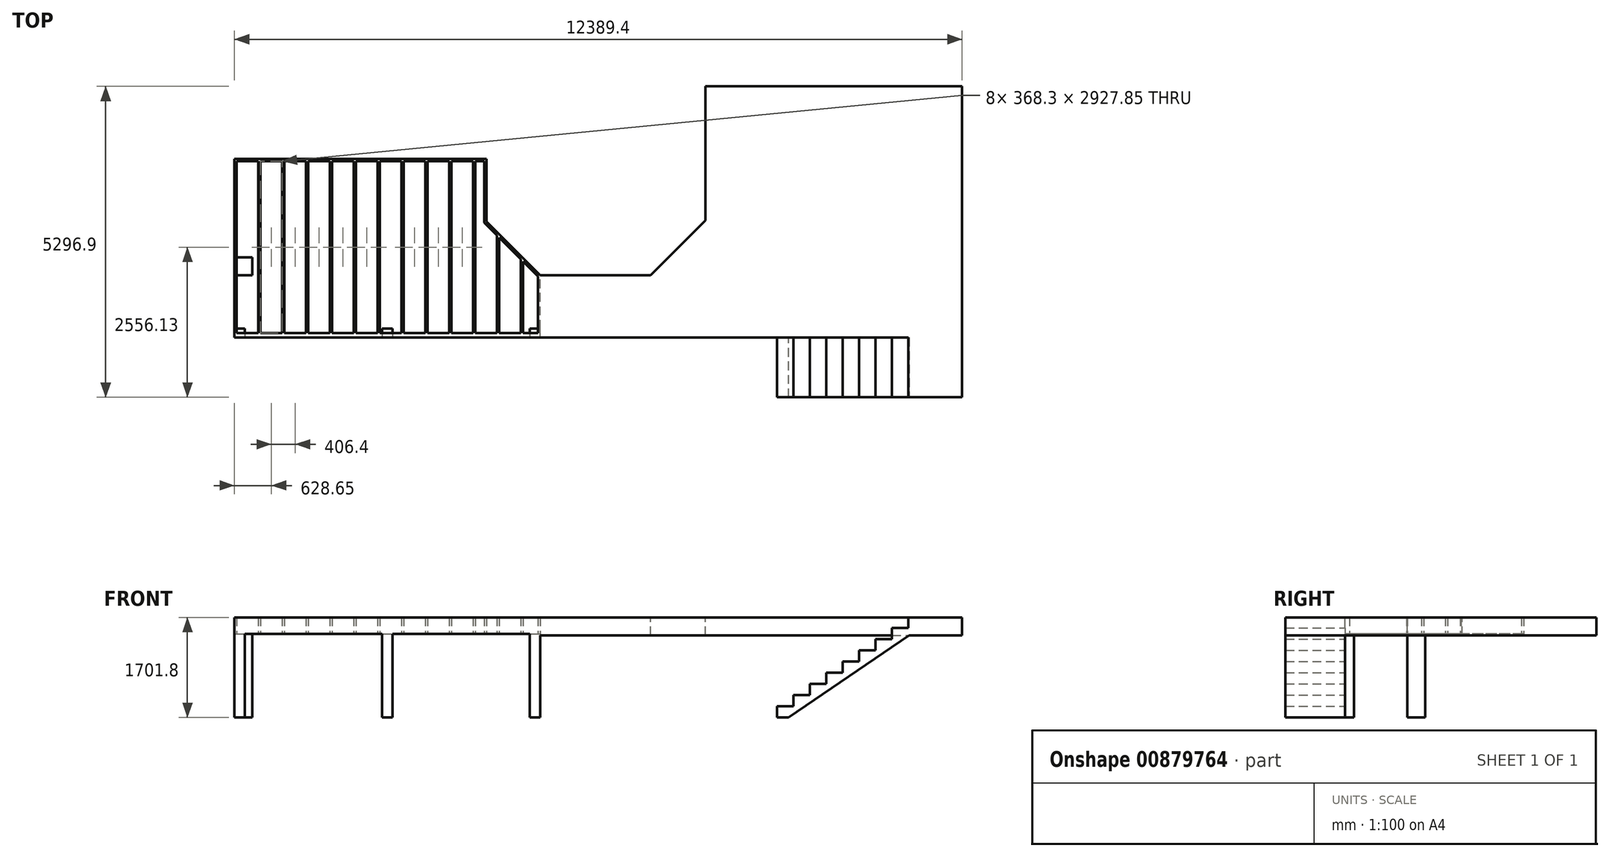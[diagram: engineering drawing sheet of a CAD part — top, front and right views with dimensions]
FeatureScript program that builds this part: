
annotation { "Feature Type Name" : "Feature", "Feature Type Description" : "" }
export const myFeature = defineFeature(function(context is Context, id is Id, definition is map)
    precondition{}
    {
        {
            var Q0;
            Q0=qCreatedBy(makeId("Top.planeOp"),FACE);
            var sketch = newSketch(context, id + "F0", { "sketchPlane" : qUnion([Q0])});
            skLineSegment(sketch, "E0.bottom", {"start": v(0, -1676.4) * mm, "end": v(304.8, -1676.4) * mm});
            skLineSegment(sketch, "E0.top", {"start": v(0, -1981.2) * mm, "end": v(304.8, -1981.2) * mm});
            skLineSegment(sketch, "E0.left", {"start": v(0, -1676.4) * mm, "end": v(0, -1981.2) * mm});
            skLineSegment(sketch, "E0.right", {"start": v(304.8, -1676.4) * mm, "end": v(304.8, -1981.2) * mm});
            skLineSegment(sketch, "E1.bottom", {"start": v(0, -2889.75) * mm, "end": v(177.8, -2889.75) * mm});
            skLineSegment(sketch, "E1.top", {"start": v(0, -3042.15) * mm, "end": v(177.8, -3042.15) * mm});
            skLineSegment(sketch, "E1.left", {"start": v(0, -2889.75) * mm, "end": v(0, -3042.15) * mm});
            skLineSegment(sketch, "E1.right", {"start": v(177.8, -2889.75) * mm, "end": v(177.8, -3042.15) * mm});
            skLineSegment(sketch, "E2.bottom", {"start": v(2514.6, -2889.75) * mm, "end": v(2692.4, -2889.75) * mm});
            skLineSegment(sketch, "E2.top", {"start": v(2514.6, -3042.15) * mm, "end": v(2692.4, -3042.15) * mm});
            skLineSegment(sketch, "E2.left", {"start": v(2514.6, -2889.75) * mm, "end": v(2514.6, -3042.15) * mm});
            skLineSegment(sketch, "E2.right", {"start": v(2692.4, -2889.75) * mm, "end": v(2692.4, -3042.15) * mm});
            skLineSegment(sketch, "E3.bottom", {"start": v(5029.2, -2889.75) * mm, "end": v(5207, -2889.75) * mm});
            skLineSegment(sketch, "E3.top", {"start": v(5029.2, -3042.15) * mm, "end": v(5207, -3042.15) * mm});
            skLineSegment(sketch, "E3.left", {"start": v(5029.2, -2889.75) * mm, "end": v(5029.2, -3042.15) * mm});
            skLineSegment(sketch, "E3.right", {"start": v(5207, -2889.75) * mm, "end": v(5207, -3042.15) * mm});
            skLineSegment(sketch, "E4", {"start": v(0, 0) * mm, "end": v(4292.6, 0) * mm, "construction": true});
            skLineSegment(sketch, "E5", {"start": v(4292.6, 0) * mm, "end": v(4292.6, -1066.8) * mm, "construction": true});
            skLineSegment(sketch, "E6", {"start": v(4292.6, -1066.8) * mm, "end": v(5226.55, -2000.75) * mm, "construction": true});
            skLineSegment(sketch, "E7", {"start": v(5226.55, -2000.75) * mm, "end": v(7106.15, -2000.75) * mm, "construction": true});
            skSolve(sketch);
        }
        {
            var Q0;
            Q0=qSketchRegion(id+"F0",true);
            extrude(context, id + "F1", {"entities" : qUnion([Q0]), "depth" : 1422.4 * mm, "offsetDistance" : 25.4 * mm});
        }
        {
            var Q0;
            Q0=makeQuery(id+"F1.opExtrude","CAP_FACE",FACE,{"disambiguationData":[OSD([sQuery(id+"F0.wireOp",EDGE,"E0.bottom"),sQuery(id+"F0.wireOp",EDGE,"E0.top"),sQuery(id+"F0.wireOp",EDGE,"E0.left"),sQuery(id+"F0.wireOp",EDGE,"E0.right")])],"isStart":false});
            var sketch = newSketch(context, id + "F2", { "sketchPlane" : qUnion([Q0])});
            skLineSegment(sketch, "E8.0", {"start": v(0, 0) * mm, "end": v(4292.6, 0) * mm});
            skLineSegment(sketch, "E9.0", {"start": v(4292.6, 0) * mm, "end": v(4292.6, -1066.8) * mm});
            skLineSegment(sketch, "E9.1", {"start": v(4292.6, -1066.8) * mm, "end": v(5207, -1981.2) * mm});
            skLineSegment(sketch, "E10", {"start": v(0, 0) * mm, "end": v(0, -3042.15) * mm});
            skLineSegment(sketch, "E11", {"start": v(0, -3042.15) * mm, "end": v(5207, -3042.15) * mm});
            skLineSegment(sketch, "E12", {"start": v(5207, -3042.15) * mm, "end": v(5207, -1981.2) * mm});
            skPoint(sketch, "E13.orphan", {"position": v(5226.55, -2000.75) * mm});
            skLineSegment(sketch, "E14.0", {"start": v(4254.5, -38.1) * mm, "end": v(4254.5, -1082.58) * mm});
            skLineSegment(sketch, "E14.1", {"start": v(5168.9, -3004.05) * mm, "end": v(5168.9, -1996.98) * mm});
            skLineSegment(sketch, "E14.2", {"start": v(38.1, -3004.05) * mm, "end": v(5168.9, -3004.05) * mm});
            skLineSegment(sketch, "E14.3", {"start": v(4254.5, -1082.58) * mm, "end": v(5168.9, -1996.98) * mm});
            skLineSegment(sketch, "E14.4", {"start": v(38.1, -38.1) * mm, "end": v(38.1, -3004.05) * mm});
            skLineSegment(sketch, "E14.5", {"start": v(38.1, -38.1) * mm, "end": v(4254.5, -38.1) * mm});
            skSolve(sketch);
        }
        {
            var Q0;
            Q0=qSketchRegion(id+"F2",true);
            extrude(context, id + "F3", {"entities" : qUnion([Q0]), "operationType" : NewBodyOperationType.ADD, "depth" : 279.4 * mm, "offsetDistance" : 25.4 * mm});
        }
        {
            var Q0;
            Q0=makeQuery(id+"F1.opExtrude","CAP_FACE",FACE,{"disambiguationData":[OSD([sQuery(id+"F0.wireOp",EDGE,"E1.bottom"),sQuery(id+"F0.wireOp",EDGE,"E1.top"),sQuery(id+"F0.wireOp",EDGE,"E1.left"),sQuery(id+"F0.wireOp",EDGE,"E1.right")])],"isStart":false});
            var sketch = newSketch(context, id + "F4", { "sketchPlane" : qUnion([Q0])});
            skPoint(sketch, "E15.oppositeSnap0", {"position": v(38.1, -2965.95) * mm});
            skLineSegment(sketch, "E15.bottom", {"start": v(38.1, -3004.05) * mm, "end": v(5168.9, -3004.05) * mm});
            skLineSegment(sketch, "E15.top", {"start": v(38.1, -2965.95) * mm, "end": v(5168.9, -2965.95) * mm});
            skLineSegment(sketch, "E15.left", {"start": v(38.1, -3004.05) * mm, "end": v(38.1, -2965.95) * mm});
            skLineSegment(sketch, "E15.right", {"start": v(5168.9, -3004.05) * mm, "end": v(5168.9, -2965.95) * mm});
            skSolve(sketch);
        }
        {
            var Q0;
            Q0=qSketchRegion(id+"F4",true);
            var Q1;
            Q1=makeQuery(id+"F3.opExtrude","CAP_FACE",FACE,{"disambiguationData":[OSD([sQuery(id+"F2.wireOp",EDGE,"E8.0"),sQuery(id+"F2.wireOp",EDGE,"E9.0"),sQuery(id+"F2.wireOp",EDGE,"E9.1"),sQuery(id+"F2.wireOp",EDGE,"E10"),sQuery(id+"F2.wireOp",EDGE,"E11"),sQuery(id+"F2.wireOp",EDGE,"E12"),sQuery(id+"F2.wireOp",EDGE,"E14.0"),sQuery(id+"F2.wireOp",EDGE,"E14.1"),sQuery(id+"F2.wireOp",EDGE,"E14.2"),sQuery(id+"F2.wireOp",EDGE,"E14.3"),sQuery(id+"F2.wireOp",EDGE,"E14.4"),sQuery(id+"F2.wireOp",EDGE,"E14.5")])],"isStart":false});
            extrude(context, id + "F5", {"entities" : qUnion([Q0]), "operationType" : NewBodyOperationType.ADD, "endBound" : BoundingType.UP_TO_SURFACE, "depth" : 25.4 * mm, "endBoundEntityFace" : qUnion([Q1]), "offsetDistance" : 25.4 * mm});
        }
        {
            var Q0;
            Q0=makeQuery(id+"F1.opExtrude","CAP_FACE",FACE,{"disambiguationData":[OSD([sQuery(id+"F0.wireOp",EDGE,"E0.bottom"),sQuery(id+"F0.wireOp",EDGE,"E0.top"),sQuery(id+"F0.wireOp",EDGE,"E0.left"),sQuery(id+"F0.wireOp",EDGE,"E0.right")])],"isStart":false});
            var sketch = newSketch(context, id + "F6", { "sketchPlane" : qUnion([Q0])});
            skLineSegment(sketch, "E16.bottom", {"start": v(406.4, -38.1) * mm, "end": v(444.5, -38.1) * mm});
            skLineSegment(sketch, "E16.top", {"start": v(406.4, -2965.95) * mm, "end": v(444.5, -2965.95) * mm});
            skLineSegment(sketch, "E16.left", {"start": v(406.4, -38.1) * mm, "end": v(406.4, -2965.95) * mm});
            skLineSegment(sketch, "E16.right", {"start": v(444.5, -38.1) * mm, "end": v(444.5, -2965.95) * mm});
            skLineSegment(sketch, "E17.1.0.0", {"start": v(850.9, -38.1) * mm, "end": v(850.9, -2965.95) * mm});
            skLineSegment(sketch, "E17.1.0.1", {"start": v(812.8, -38.1) * mm, "end": v(812.8, -2965.95) * mm});
            skLineSegment(sketch, "E17.1.0.2", {"start": v(812.8, -38.1) * mm, "end": v(850.9, -38.1) * mm});
            skLineSegment(sketch, "E17.1.0.3", {"start": v(812.8, -2965.95) * mm, "end": v(850.9, -2965.95) * mm});
            skLineSegment(sketch, "E17.2.0.0", {"start": v(1257.3, -38.1) * mm, "end": v(1257.3, -2965.95) * mm});
            skLineSegment(sketch, "E17.2.0.1", {"start": v(1219.2, -38.1) * mm, "end": v(1219.2, -2965.95) * mm});
            skLineSegment(sketch, "E17.2.0.2", {"start": v(1219.2, -38.1) * mm, "end": v(1257.3, -38.1) * mm});
            skLineSegment(sketch, "E17.2.0.3", {"start": v(1219.2, -2965.95) * mm, "end": v(1257.3, -2965.95) * mm});
            skLineSegment(sketch, "E17.3.0.0", {"start": v(1663.7, -38.1) * mm, "end": v(1663.7, -2965.95) * mm});
            skLineSegment(sketch, "E17.3.0.1", {"start": v(1625.6, -38.1) * mm, "end": v(1625.6, -2965.95) * mm});
            skLineSegment(sketch, "E17.3.0.2", {"start": v(1625.6, -38.1) * mm, "end": v(1663.7, -38.1) * mm});
            skLineSegment(sketch, "E17.3.0.3", {"start": v(1625.6, -2965.95) * mm, "end": v(1663.7, -2965.95) * mm});
            skLineSegment(sketch, "E17.4.0.0", {"start": v(2070.1, -38.1) * mm, "end": v(2070.1, -2965.95) * mm});
            skLineSegment(sketch, "E17.4.0.1", {"start": v(2032, -38.1) * mm, "end": v(2032, -2965.95) * mm});
            skLineSegment(sketch, "E17.4.0.2", {"start": v(2032, -38.1) * mm, "end": v(2070.1, -38.1) * mm});
            skLineSegment(sketch, "E17.4.0.3", {"start": v(2032, -2965.95) * mm, "end": v(2070.1, -2965.95) * mm});
            skLineSegment(sketch, "E17.5.0.0", {"start": v(2476.5, -38.1) * mm, "end": v(2476.5, -2965.95) * mm});
            skLineSegment(sketch, "E17.5.0.1", {"start": v(2438.4, -38.1) * mm, "end": v(2438.4, -2965.95) * mm});
            skLineSegment(sketch, "E17.5.0.2", {"start": v(2438.4, -38.1) * mm, "end": v(2476.5, -38.1) * mm});
            skLineSegment(sketch, "E17.5.0.3", {"start": v(2438.4, -2965.95) * mm, "end": v(2476.5, -2965.95) * mm});
            skLineSegment(sketch, "E17.6.0.0", {"start": v(2882.9, -38.1) * mm, "end": v(2882.9, -2965.95) * mm});
            skLineSegment(sketch, "E17.6.0.1", {"start": v(2844.8, -38.1) * mm, "end": v(2844.8, -2965.95) * mm});
            skLineSegment(sketch, "E17.6.0.2", {"start": v(2844.8, -38.1) * mm, "end": v(2882.9, -38.1) * mm});
            skLineSegment(sketch, "E17.6.0.3", {"start": v(2844.8, -2965.95) * mm, "end": v(2882.9, -2965.95) * mm});
            skLineSegment(sketch, "E17.7.0.0", {"start": v(3289.3, -38.1) * mm, "end": v(3289.3, -2965.95) * mm});
            skLineSegment(sketch, "E17.7.0.1", {"start": v(3251.2, -38.1) * mm, "end": v(3251.2, -2965.95) * mm});
            skLineSegment(sketch, "E17.7.0.2", {"start": v(3251.2, -38.1) * mm, "end": v(3289.3, -38.1) * mm});
            skLineSegment(sketch, "E17.7.0.3", {"start": v(3251.2, -2965.95) * mm, "end": v(3289.3, -2965.95) * mm});
            skLineSegment(sketch, "E17.8.0.0", {"start": v(3695.7, -38.1) * mm, "end": v(3695.7, -2965.95) * mm});
            skLineSegment(sketch, "E17.8.0.1", {"start": v(3657.6, -38.1) * mm, "end": v(3657.6, -2965.95) * mm});
            skLineSegment(sketch, "E17.8.0.2", {"start": v(3657.6, -38.1) * mm, "end": v(3695.7, -38.1) * mm});
            skLineSegment(sketch, "E17.8.0.3", {"start": v(3657.6, -2965.95) * mm, "end": v(3695.7, -2965.95) * mm});
            skLineSegment(sketch, "E17.9.0.0", {"start": v(4102.1, -38.1) * mm, "end": v(4102.1, -2965.95) * mm});
            skLineSegment(sketch, "E17.9.0.1", {"start": v(4064, -38.1) * mm, "end": v(4064, -2965.95) * mm});
            skLineSegment(sketch, "E17.9.0.2", {"start": v(4064, -38.1) * mm, "end": v(4102.1, -38.1) * mm});
            skLineSegment(sketch, "E17.9.0.3", {"start": v(4064, -2965.95) * mm, "end": v(4102.1, -2965.95) * mm});
            skLineSegment(sketch, "E17.direction1", {"start": v(406.4, -2965.95) * mm, "end": v(812.8, -2965.95) * mm, "construction": true});
            skLineSegment(sketch, "E18.top", {"start": v(4470.4, -2965.95) * mm, "end": v(4508.5, -2965.95) * mm});
            skLineSegment(sketch, "E18.left", {"start": v(4470.4, -1298.48) * mm, "end": v(4470.4, -2965.95) * mm});
            skLineSegment(sketch, "E18.right", {"start": v(4508.5, -1336.58) * mm, "end": v(4508.5, -2965.95) * mm});
            skLineSegment(sketch, "E19.top", {"start": v(4876.8, -2965.95) * mm, "end": v(4914.9, -2965.95) * mm});
            skLineSegment(sketch, "E19.left", {"start": v(4876.8, -1704.88) * mm, "end": v(4876.8, -2965.95) * mm});
            skLineSegment(sketch, "E19.right", {"start": v(4914.9, -1742.98) * mm, "end": v(4914.9, -2965.95) * mm});
            skLineSegment(sketch, "E20", {"start": v(4470.4, -1298.48) * mm, "end": v(4508.5, -1336.58) * mm});
            skLineSegment(sketch, "E21.trimOffspring", {"start": v(4876.8, -1704.88) * mm, "end": v(4914.9, -1742.98) * mm});
            skSolve(sketch);
        }
        {
            var Q0;
            Q0=qSketchRegion(id+"F6",true);
            var Q1;
            {var subQ0=sQuery(id+"F2.wireOp",EDGE,"E14.5");var subQ1=sQuery(id+"F2.wireOp",EDGE,"E14.4");var subQ2=sQuery(id+"F2.wireOp",EDGE,"E14.3");var subQ3=sQuery(id+"F2.wireOp",EDGE,"E14.2");var subQ4=sQuery(id+"F2.wireOp",EDGE,"E14.1");var subQ5=sQuery(id+"F2.wireOp",EDGE,"E14.0");var subQ6=sQuery(id+"F2.wireOp",EDGE,"E12");var subQ7=sQuery(id+"F2.wireOp",EDGE,"E11");var subQ8=sQuery(id+"F2.wireOp",EDGE,"E10");var subQ9=sQuery(id+"F2.wireOp",EDGE,"E9.1");var subQ10=sQuery(id+"F2.wireOp",EDGE,"E9.0");var subQ11=sQuery(id+"F2.wireOp",EDGE,"E8.0");Q1=makeQuery(id+"F5.boolean.opBoolean","MERGE",FACE,{"derivedFrom":[makeQuery(id+"F3.opExtrude","CAP_FACE",FACE,{"disambiguationData":[OSD([subQ11,subQ10,subQ9,subQ8,subQ7,subQ6,subQ5,subQ4,subQ3,subQ2,subQ1,subQ0])],"isStart":false}),makeQuery(id+"F5.opExtrude","CAP_FACE",FACE,{"disambiguationData":[OSD([subQ11,subQ10,subQ9,subQ8,subQ7,subQ6,subQ5,subQ4,subQ3,subQ2,subQ1,subQ0])],"isStart":false})]});}
            extrude(context, id + "F7", {"entities" : qUnion([Q0]), "operationType" : NewBodyOperationType.ADD, "endBound" : BoundingType.UP_TO_SURFACE, "depth" : 25.4 * mm, "endBoundEntityFace" : qUnion([Q1]), "offsetDistance" : 25.4 * mm});
        }
        {
            var Q0;
            Q0=makeQuery(id+"F7.boolean.opBoolean","MERGE",FACE,{"derivedFrom":[makeQuery(id+"F5.boolean.opBoolean","MERGE",FACE,{"derivedFrom":[makeQuery(id+"F3.opExtrude","CAP_FACE",FACE,{"disambiguationData":[OSD([sQuery(id+"F2.wireOp",EDGE,"E8.0"),sQuery(id+"F2.wireOp",EDGE,"E9.0"),sQuery(id+"F2.wireOp",EDGE,"E9.1"),sQuery(id+"F2.wireOp",EDGE,"E10"),sQuery(id+"F2.wireOp",EDGE,"E11"),sQuery(id+"F2.wireOp",EDGE,"E12"),sQuery(id+"F2.wireOp",EDGE,"E14.0"),sQuery(id+"F2.wireOp",EDGE,"E14.1"),sQuery(id+"F2.wireOp",EDGE,"E14.2"),sQuery(id+"F2.wireOp",EDGE,"E14.3"),sQuery(id+"F2.wireOp",EDGE,"E14.4"),sQuery(id+"F2.wireOp",EDGE,"E14.5")])],"isStart":false}),makeQuery(id+"F5.opExtrude","CAP_FACE",FACE,{"disambiguationData":[OSD([sQuery(id+"F4.wireOp",EDGE,"E15.bottom"),sQuery(id+"F4.wireOp",EDGE,"E15.top"),sQuery(id+"F4.wireOp",EDGE,"E15.left"),sQuery(id+"F4.wireOp",EDGE,"E15.right")])],"isStart":false})]}),makeQuery(id+"F7.opExtrude","CAP_FACE",FACE,{"disambiguationData":[OSD([sQuery(id+"F6.wireOp",EDGE,"E16.bottom"),sQuery(id+"F6.wireOp",EDGE,"E16.top"),sQuery(id+"F6.wireOp",EDGE,"E16.left"),sQuery(id+"F6.wireOp",EDGE,"E16.right")])],"isStart":false}),makeQuery(id+"F7.opExtrude","CAP_FACE",FACE,{"disambiguationData":[OSD([sQuery(id+"F6.wireOp",EDGE,"E17.1.0.0"),sQuery(id+"F6.wireOp",EDGE,"E17.1.0.1"),sQuery(id+"F6.wireOp",EDGE,"E17.1.0.2"),sQuery(id+"F6.wireOp",EDGE,"E17.1.0.3")])],"isStart":false}),makeQuery(id+"F7.opExtrude","CAP_FACE",FACE,{"disambiguationData":[OSD([sQuery(id+"F6.wireOp",EDGE,"E17.2.0.0"),sQuery(id+"F6.wireOp",EDGE,"E17.2.0.1"),sQuery(id+"F6.wireOp",EDGE,"E17.2.0.2"),sQuery(id+"F6.wireOp",EDGE,"E17.2.0.3")])],"isStart":false}),makeQuery(id+"F7.opExtrude","CAP_FACE",FACE,{"disambiguationData":[OSD([sQuery(id+"F6.wireOp",EDGE,"E17.3.0.0"),sQuery(id+"F6.wireOp",EDGE,"E17.3.0.1"),sQuery(id+"F6.wireOp",EDGE,"E17.3.0.2"),sQuery(id+"F6.wireOp",EDGE,"E17.3.0.3")])],"isStart":false}),makeQuery(id+"F7.opExtrude","CAP_FACE",FACE,{"disambiguationData":[OSD([sQuery(id+"F6.wireOp",EDGE,"E17.4.0.0"),sQuery(id+"F6.wireOp",EDGE,"E17.4.0.1"),sQuery(id+"F6.wireOp",EDGE,"E17.4.0.2"),sQuery(id+"F6.wireOp",EDGE,"E17.4.0.3")])],"isStart":false}),makeQuery(id+"F7.opExtrude","CAP_FACE",FACE,{"disambiguationData":[OSD([sQuery(id+"F6.wireOp",EDGE,"E17.5.0.0"),sQuery(id+"F6.wireOp",EDGE,"E17.5.0.1"),sQuery(id+"F6.wireOp",EDGE,"E17.5.0.2"),sQuery(id+"F6.wireOp",EDGE,"E17.5.0.3")])],"isStart":false}),makeQuery(id+"F7.opExtrude","CAP_FACE",FACE,{"disambiguationData":[OSD([sQuery(id+"F6.wireOp",EDGE,"E17.6.0.0"),sQuery(id+"F6.wireOp",EDGE,"E17.6.0.1"),sQuery(id+"F6.wireOp",EDGE,"E17.6.0.2"),sQuery(id+"F6.wireOp",EDGE,"E17.6.0.3")])],"isStart":false}),makeQuery(id+"F7.opExtrude","CAP_FACE",FACE,{"disambiguationData":[OSD([sQuery(id+"F6.wireOp",EDGE,"E17.7.0.0"),sQuery(id+"F6.wireOp",EDGE,"E17.7.0.1"),sQuery(id+"F6.wireOp",EDGE,"E17.7.0.2"),sQuery(id+"F6.wireOp",EDGE,"E17.7.0.3")])],"isStart":false}),makeQuery(id+"F7.opExtrude","CAP_FACE",FACE,{"disambiguationData":[OSD([sQuery(id+"F6.wireOp",EDGE,"E17.8.0.0"),sQuery(id+"F6.wireOp",EDGE,"E17.8.0.1"),sQuery(id+"F6.wireOp",EDGE,"E17.8.0.2"),sQuery(id+"F6.wireOp",EDGE,"E17.8.0.3")])],"isStart":false}),makeQuery(id+"F7.opExtrude","CAP_FACE",FACE,{"disambiguationData":[OSD([sQuery(id+"F6.wireOp",EDGE,"E17.9.0.0"),sQuery(id+"F6.wireOp",EDGE,"E17.9.0.1"),sQuery(id+"F6.wireOp",EDGE,"E17.9.0.2"),sQuery(id+"F6.wireOp",EDGE,"E17.9.0.3")])],"isStart":false}),makeQuery(id+"F7.opExtrude","CAP_FACE",FACE,{"disambiguationData":[OSD([sQuery(id+"F6.wireOp",EDGE,"E18.top"),sQuery(id+"F6.wireOp",EDGE,"E18.left"),sQuery(id+"F6.wireOp",EDGE,"E18.right"),sQuery(id+"F6.wireOp",EDGE,"E20")])],"isStart":false}),makeQuery(id+"F7.opExtrude","CAP_FACE",FACE,{"disambiguationData":[OSD([sQuery(id+"F6.wireOp",EDGE,"E19.top"),sQuery(id+"F6.wireOp",EDGE,"E19.left"),sQuery(id+"F6.wireOp",EDGE,"E19.right"),sQuery(id+"F6.wireOp",EDGE,"E21.trimOffspring")])],"isStart":false})]});
            var sketch = newSketch(context, id + "F8", { "sketchPlane" : qUnion([Q0])});
            skLineSegment(sketch, "E22", {"start": v(5207, -1981.2) * mm, "end": v(5207, -3042.15) * mm});
            skLineSegment(sketch, "E23", {"start": v(5207, -1981.2) * mm, "end": v(7086.6, -1981.2) * mm});
            skLineSegment(sketch, "E24", {"start": v(7086.6, -1981.2) * mm, "end": v(8020.55, -1047.25) * mm});
            skLineSegment(sketch, "E25", {"start": v(8020.55, -1047.25) * mm, "end": v(8020.55, 1238.75) * mm});
            skLineSegment(sketch, "E26", {"start": v(8020.55, 1238.75) * mm, "end": v(12389.35, 1238.75) * mm});
            skLineSegment(sketch, "E27", {"start": v(12389.35, 1238.75) * mm, "end": v(12389.35, -3042.15) * mm});
            skLineSegment(sketch, "E28", {"start": v(5207, -3042.15) * mm, "end": v(12389.35, -3042.15) * mm});
            skSolve(sketch);
        }
        {
            var Q0;
            Q0=qSketchRegion(id+"F8",true);
            extrude(context, id + "F9", {"entities" : qUnion([Q0]), "operationType" : NewBodyOperationType.ADD, "oppositeDirection" : true, "depth" : 304.8 * mm, "offsetDistance" : 25.4 * mm});
        }
        {
            var Q0;
            Q0=makeQuery(id+"F9.boolean.opBoolean","MERGE",FACE,{"derivedFrom":[makeQuery(id+"F7.boolean.opBoolean","MERGE",FACE,{"derivedFrom":[makeQuery(id+"F5.boolean.opBoolean","MERGE",FACE,{"derivedFrom":[makeQuery(id+"F3.opExtrude","CAP_FACE",FACE,{"disambiguationData":[OSD([sQuery(id+"F2.wireOp",EDGE,"E8.0"),sQuery(id+"F2.wireOp",EDGE,"E9.0"),sQuery(id+"F2.wireOp",EDGE,"E9.1"),sQuery(id+"F2.wireOp",EDGE,"E10"),sQuery(id+"F2.wireOp",EDGE,"E11"),sQuery(id+"F2.wireOp",EDGE,"E12"),sQuery(id+"F2.wireOp",EDGE,"E14.0"),sQuery(id+"F2.wireOp",EDGE,"E14.1"),sQuery(id+"F2.wireOp",EDGE,"E14.2"),sQuery(id+"F2.wireOp",EDGE,"E14.3"),sQuery(id+"F2.wireOp",EDGE,"E14.4"),sQuery(id+"F2.wireOp",EDGE,"E14.5")])],"isStart":false}),makeQuery(id+"F5.opExtrude","CAP_FACE",FACE,{"disambiguationData":[OSD([sQuery(id+"F4.wireOp",EDGE,"E15.bottom"),sQuery(id+"F4.wireOp",EDGE,"E15.top"),sQuery(id+"F4.wireOp",EDGE,"E15.left"),sQuery(id+"F4.wireOp",EDGE,"E15.right")])],"isStart":false})]}),makeQuery(id+"F7.opExtrude","CAP_FACE",FACE,{"disambiguationData":[OSD([sQuery(id+"F6.wireOp",EDGE,"E16.bottom"),sQuery(id+"F6.wireOp",EDGE,"E16.top"),sQuery(id+"F6.wireOp",EDGE,"E16.left"),sQuery(id+"F6.wireOp",EDGE,"E16.right")])],"isStart":false}),makeQuery(id+"F7.opExtrude","CAP_FACE",FACE,{"disambiguationData":[OSD([sQuery(id+"F6.wireOp",EDGE,"E17.1.0.0"),sQuery(id+"F6.wireOp",EDGE,"E17.1.0.1"),sQuery(id+"F6.wireOp",EDGE,"E17.1.0.2"),sQuery(id+"F6.wireOp",EDGE,"E17.1.0.3")])],"isStart":false}),makeQuery(id+"F7.opExtrude","CAP_FACE",FACE,{"disambiguationData":[OSD([sQuery(id+"F6.wireOp",EDGE,"E17.2.0.0"),sQuery(id+"F6.wireOp",EDGE,"E17.2.0.1"),sQuery(id+"F6.wireOp",EDGE,"E17.2.0.2"),sQuery(id+"F6.wireOp",EDGE,"E17.2.0.3")])],"isStart":false}),makeQuery(id+"F7.opExtrude","CAP_FACE",FACE,{"disambiguationData":[OSD([sQuery(id+"F6.wireOp",EDGE,"E17.3.0.0"),sQuery(id+"F6.wireOp",EDGE,"E17.3.0.1"),sQuery(id+"F6.wireOp",EDGE,"E17.3.0.2"),sQuery(id+"F6.wireOp",EDGE,"E17.3.0.3")])],"isStart":false}),makeQuery(id+"F7.opExtrude","CAP_FACE",FACE,{"disambiguationData":[OSD([sQuery(id+"F6.wireOp",EDGE,"E17.4.0.0"),sQuery(id+"F6.wireOp",EDGE,"E17.4.0.1"),sQuery(id+"F6.wireOp",EDGE,"E17.4.0.2"),sQuery(id+"F6.wireOp",EDGE,"E17.4.0.3")])],"isStart":false}),makeQuery(id+"F7.opExtrude","CAP_FACE",FACE,{"disambiguationData":[OSD([sQuery(id+"F6.wireOp",EDGE,"E17.5.0.0"),sQuery(id+"F6.wireOp",EDGE,"E17.5.0.1"),sQuery(id+"F6.wireOp",EDGE,"E17.5.0.2"),sQuery(id+"F6.wireOp",EDGE,"E17.5.0.3")])],"isStart":false}),makeQuery(id+"F7.opExtrude","CAP_FACE",FACE,{"disambiguationData":[OSD([sQuery(id+"F6.wireOp",EDGE,"E17.6.0.0"),sQuery(id+"F6.wireOp",EDGE,"E17.6.0.1"),sQuery(id+"F6.wireOp",EDGE,"E17.6.0.2"),sQuery(id+"F6.wireOp",EDGE,"E17.6.0.3")])],"isStart":false}),makeQuery(id+"F7.opExtrude","CAP_FACE",FACE,{"disambiguationData":[OSD([sQuery(id+"F6.wireOp",EDGE,"E17.7.0.0"),sQuery(id+"F6.wireOp",EDGE,"E17.7.0.1"),sQuery(id+"F6.wireOp",EDGE,"E17.7.0.2"),sQuery(id+"F6.wireOp",EDGE,"E17.7.0.3")])],"isStart":false}),makeQuery(id+"F7.opExtrude","CAP_FACE",FACE,{"disambiguationData":[OSD([sQuery(id+"F6.wireOp",EDGE,"E17.8.0.0"),sQuery(id+"F6.wireOp",EDGE,"E17.8.0.1"),sQuery(id+"F6.wireOp",EDGE,"E17.8.0.2"),sQuery(id+"F6.wireOp",EDGE,"E17.8.0.3")])],"isStart":false}),makeQuery(id+"F7.opExtrude","CAP_FACE",FACE,{"disambiguationData":[OSD([sQuery(id+"F6.wireOp",EDGE,"E17.9.0.0"),sQuery(id+"F6.wireOp",EDGE,"E17.9.0.1"),sQuery(id+"F6.wireOp",EDGE,"E17.9.0.2"),sQuery(id+"F6.wireOp",EDGE,"E17.9.0.3")])],"isStart":false}),makeQuery(id+"F7.opExtrude","CAP_FACE",FACE,{"disambiguationData":[OSD([sQuery(id+"F6.wireOp",EDGE,"E18.top"),sQuery(id+"F6.wireOp",EDGE,"E18.left"),sQuery(id+"F6.wireOp",EDGE,"E18.right"),sQuery(id+"F6.wireOp",EDGE,"E20")])],"isStart":false}),makeQuery(id+"F7.opExtrude","CAP_FACE",FACE,{"disambiguationData":[OSD([sQuery(id+"F6.wireOp",EDGE,"E19.top"),sQuery(id+"F6.wireOp",EDGE,"E19.left"),sQuery(id+"F6.wireOp",EDGE,"E19.right"),sQuery(id+"F6.wireOp",EDGE,"E21.trimOffspring")])],"isStart":false})]}),makeQuery(id+"F9.opExtrude","CAP_FACE",FACE,{"disambiguationData":[OSD([sQuery(id+"F8.wireOp",EDGE,"E22"),sQuery(id+"F8.wireOp",EDGE,"E23"),sQuery(id+"F8.wireOp",EDGE,"E24"),sQuery(id+"F8.wireOp",EDGE,"E25"),sQuery(id+"F8.wireOp",EDGE,"E26"),sQuery(id+"F8.wireOp",EDGE,"E27"),sQuery(id+"F8.wireOp",EDGE,"E28")])],"isStart":true})]});
            var sketch = newSketch(context, id + "F10", { "sketchPlane" : qUnion([Q0])});
            skLineSegment(sketch, "E29.bottom", {"start": v(12389.35, -3042.15) * mm, "end": v(11474.95, -3042.15) * mm});
            skLineSegment(sketch, "E29.top", {"start": v(12389.35, -4058.15) * mm, "end": v(11474.95, -4058.15) * mm});
            skLineSegment(sketch, "E29.left", {"start": v(12389.35, -3042.15) * mm, "end": v(12389.35, -4058.15) * mm});
            skLineSegment(sketch, "E29.right", {"start": v(11474.95, -3042.15) * mm, "end": v(11474.95, -4058.15) * mm});
            skSolve(sketch);
        }
        {
            var Q0;
            Q0=qSketchRegion(id+"F10",true);
            var Q1;
            Q1=makeQuery(id+"F9.opExtrude","CAP_FACE",FACE,{"disambiguationData":[OSD([sQuery(id+"F8.wireOp",EDGE,"E22"),sQuery(id+"F8.wireOp",EDGE,"E23"),sQuery(id+"F8.wireOp",EDGE,"E24"),sQuery(id+"F8.wireOp",EDGE,"E25"),sQuery(id+"F8.wireOp",EDGE,"E26"),sQuery(id+"F8.wireOp",EDGE,"E27"),sQuery(id+"F8.wireOp",EDGE,"E28")])],"isStart":false});
            extrude(context, id + "F11", {"entities" : qUnion([Q0]), "operationType" : NewBodyOperationType.ADD, "endBound" : BoundingType.UP_TO_SURFACE, "oppositeDirection" : true, "depth" : 25.4 * mm, "endBoundEntityFace" : qUnion([Q1]), "offsetDistance" : 25.4 * mm});
        }
        {
            var Q0;
            Q0=makeQuery(id+"F9.boolean.opBoolean","MERGE",FACE,{"derivedFrom":[makeQuery(id+"F3.boolean.opBoolean","MERGE",FACE,{"derivedFrom":[makeQuery(id+"F1.opExtrude","SWEPT_FACE",FACE,{"disambiguationData":[OSD([sQuery(id+"F0.wireOp",EDGE,"E1.top")])]}),makeQuery(id+"F1.opExtrude","SWEPT_FACE",FACE,{"disambiguationData":[OSD([sQuery(id+"F0.wireOp",EDGE,"E2.top")])]}),makeQuery(id+"F1.opExtrude","SWEPT_FACE",FACE,{"disambiguationData":[OSD([sQuery(id+"F0.wireOp",EDGE,"E3.top")])]}),makeQuery(id+"F3.opExtrude","SWEPT_FACE",FACE,{"disambiguationData":[OSD([sQuery(id+"F2.wireOp",EDGE,"E11")])]})]}),makeQuery(id+"F9.opExtrude","SWEPT_FACE",FACE,{"disambiguationData":[OSD([sQuery(id+"F8.wireOp",EDGE,"E28")])]})]});
            var sketch = newSketch(context, id + "F12", { "sketchPlane" : qUnion([Q0])});
            skLineSegment(sketch, "E30", {"start": v(11195.55, 1524) * mm, "end": v(11474.95, 1524) * mm});
            skLineSegment(sketch, "E31", {"start": v(11195.55, 1524) * mm, "end": v(11195.55, 1333.5) * mm});
            skLineSegment(sketch, "E32", {"start": v(10916.15, 1333.5) * mm, "end": v(11195.55, 1333.5) * mm});
            skLineSegment(sketch, "E33", {"start": v(10916.15, 1333.5) * mm, "end": v(10916.15, 1143) * mm});
            skLineSegment(sketch, "E34", {"start": v(10636.75, 1143) * mm, "end": v(10916.15, 1143) * mm});
            skLineSegment(sketch, "E35", {"start": v(10636.75, 1143) * mm, "end": v(10636.75, 952.5) * mm});
            skLineSegment(sketch, "E36", {"start": v(10357.35, 952.5) * mm, "end": v(10636.75, 952.5) * mm});
            skLineSegment(sketch, "E37", {"start": v(10357.35, 952.5) * mm, "end": v(10357.35, 762) * mm});
            skLineSegment(sketch, "E38", {"start": v(10077.95, 762) * mm, "end": v(10357.35, 762) * mm});
            skLineSegment(sketch, "E39", {"start": v(10077.95, 762) * mm, "end": v(10077.95, 571.5) * mm});
            skLineSegment(sketch, "E40", {"start": v(9798.55, 571.5) * mm, "end": v(10077.95, 571.5) * mm});
            skLineSegment(sketch, "E41", {"start": v(9798.55, 571.5) * mm, "end": v(9798.55, 381) * mm});
            skLineSegment(sketch, "E42", {"start": v(9519.15, 381) * mm, "end": v(9798.55, 381) * mm});
            skLineSegment(sketch, "E43", {"start": v(9519.15, 381) * mm, "end": v(9519.15, 190.5) * mm});
            skLineSegment(sketch, "E44", {"start": v(9239.75, 190.5) * mm, "end": v(9519.15, 190.5) * mm});
            skLineSegment(sketch, "E45", {"start": v(9434.62, 0) * mm, "end": v(9239.75, 0) * mm});
            skLineSegment(sketch, "E46", {"start": v(9239.75, 190.5) * mm, "end": v(11195.55, 1524) * mm, "construction": true});
            skPoint(sketch, "E47", {"position": v(9337.18, 0) * mm});
            skLineSegment(sketch, "E48", {"start": v(9239.75, 190.5) * mm, "end": v(9239.75, 0) * mm});
            skLineSegment(sketch, "E49", {"start": v(9434.62, 0) * mm, "end": v(11930.6, 1701.8) * mm});
            skLineSegment(sketch, "E50", {"start": v(11930.6, 1701.8) * mm, "end": v(11474.95, 1701.8) * mm});
            skLineSegment(sketch, "E51", {"start": v(11474.95, 1701.8) * mm, "end": v(11474.95, 1524) * mm});
            skSolve(sketch);
        }
        {
            var Q0;
            Q0=qSketchRegion(id+"F12",true);
            var Q1;
            Q1=makeQuery(id+"F11.opExtrude","SWEPT_FACE",FACE,{"disambiguationData":[OSD([sQuery(id+"F10.wireOp",EDGE,"E29.top")])]});
            extrude(context, id + "F13", {"entities" : qUnion([Q0]), "operationType" : NewBodyOperationType.ADD, "endBound" : BoundingType.UP_TO_SURFACE, "depth" : 25.4 * mm, "endBoundEntityFace" : qUnion([Q1]), "offsetDistance" : 25.4 * mm});
        }
    });
